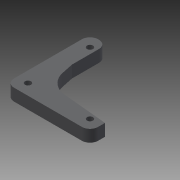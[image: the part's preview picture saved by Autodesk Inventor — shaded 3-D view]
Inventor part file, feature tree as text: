
AUTODESK INVENTOR PART (.ipt)
format: ipt  version: 2013 (Build 170138000, 138)  size: 96,256 bytes
history: native  units: mm
features: extrude x1, sketch x1
ambient origin geometry x8: Origin, YZ Plane, XZ Plane, XY Plane, X Axis, Y Axis, Z Axis, Center Point
bodies: Solid1 (feature_tree)
feature tree (2):
  extrude  "Extrusion1"  [1 undecoded]
  sketch  "Sketch1"  dims[d0=6.0mm d1=0.0mm]
note: 1 required parameter value undecoded (feature->parameter linkage not recoverable at this tier; creation-order binding heuristic only, values carry confidence <= 0.55)
